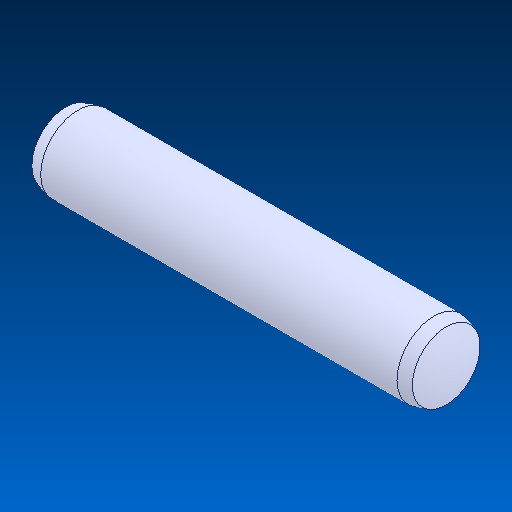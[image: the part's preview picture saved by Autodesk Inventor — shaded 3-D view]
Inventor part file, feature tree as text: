
AUTODESK INVENTOR PART (.ipt)
format: ipt  version: 2022.2 (Build 262287000, 287)  size: 100,352 bytes
history: native  units: in
note: dims shown in document units (in); Inventor stores cm internally (conversion verified against a paired STEP export)
features: mirror x1
ambient origin geometry x8: Origin, YZ Plane, XZ Plane, XY Plane, X Axis, Y Axis, Z Axis, Center Point
bodies: Solid1 (feature_tree)
feature tree (1):
  mirror  "Mirror1"
